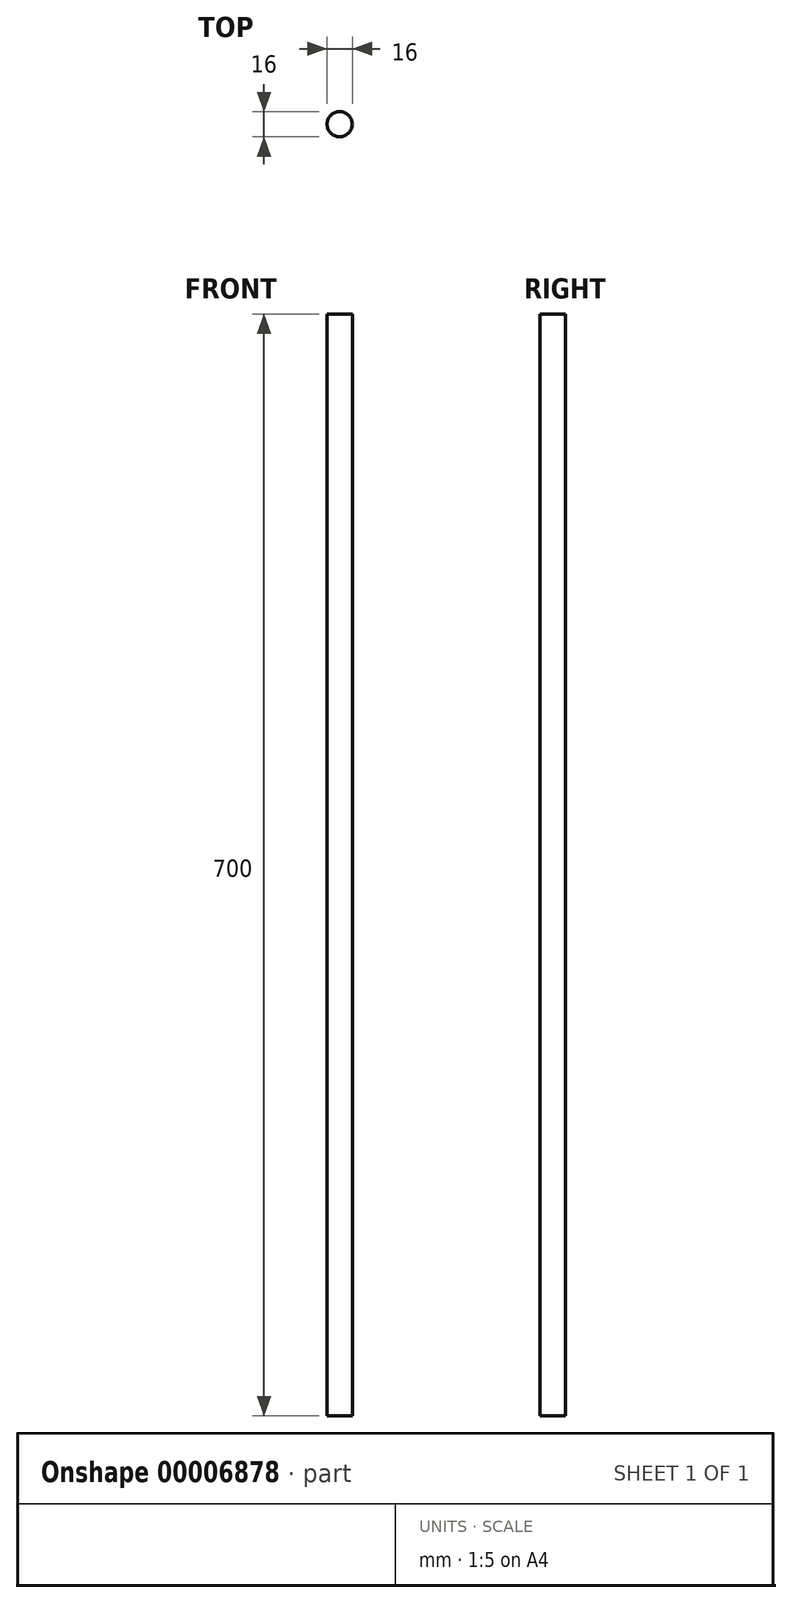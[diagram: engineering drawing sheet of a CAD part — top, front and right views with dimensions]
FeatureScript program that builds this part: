
annotation { "Feature Type Name" : "Feature", "Feature Type Description" : "" }
export const myFeature = defineFeature(function(context is Context, id is Id, definition is map)
    precondition{}
    {
        {
            var Q0;
            Q0=qCreatedBy(makeId("Top.planeOp"),FACE);
            var sketch = newSketch(context, id + "F0", { "sketchPlane" : qUnion([Q0])});
            skCircle(sketch, "E0", {"center": v(0, 0) * mm, "radius": 8 * mm});
            skSolve(sketch);
        }
        {
            var Q0;
            Q0=qSketchRegion(id+"F0",true);
            extrude(context, id + "F1", {"entities" : qUnion([Q0]), "depth" : (700) * mm});
        }
    });
